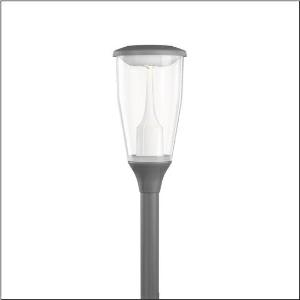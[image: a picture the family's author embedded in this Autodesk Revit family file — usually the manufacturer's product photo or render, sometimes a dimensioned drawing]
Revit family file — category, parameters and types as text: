
# Revit family: dl_11_iq___st1_2a_5xa5565ef14h000022_473d
name_source: partatom
category: Lighting Fixtures
units: mm (PartAtom-declared; Revit-internal decimal feet)

## family parameters
Cut with Voids When Loaded = No
Host = Face
Light Source = No
Part Type = Normal
Room Calculation Point = No
Round Connector Dimension = Use Diameter
Shared = No

## types (1)
- --- (1 x LED, 1560 lm, 10.5 W, 3000K)
    Apparent Load = 11 VA
    CIE Flux Codes = 24 63 94 96 100
    Color Rendering = 70
    Color Temperature = 3000K
    Default Elevation = 1800 mm
    Description = DL 11 iQ, mast luminaire, Module 540 iQ-SR, primary light control with 3 zone facetted reflector, of plastic, silver coated, highly specular, structured, primary optical cover: cover, of PMMA, transparent, light distribution: ST1.2a, light emission: direct distribution, primary light characteristic: asymmetric, installation type: post-top, LED, High Power LED, rated luminous flux: 1.560lm, luminous efficacy: 149lm/W, light colour: 730, colour temperature: 3000K, control: Street-Remote, Auto-Match, Temp-Guard, Lumen-Switch, Night-Set, Smart-Wire, Light-Fading, Desk-Remote (wireless, voltage-free reading and setting of iQ features in the workshop via application-optimized NFC function/RFID function), optimised constant luminous flux control (CLO 2.0), mains connection: 220..240V, AC, 50/60Hz, connection cable pre-assembled, cable length: 5,5m, start of lifetime: 10W, end of service life: 11W, reduction: 5W, luminaire housing, upper part, of diecast aluminium, coated, Siteco® metallic grey (DB 702S), spigot size: 60mm (post-top), post-top mast mounting element, of diecast aluminium, coated, Siteco® metallic grey (DB 702S), Module 540 iQ-SR, traffic white (RAL 9016), equipment: standard, protection rating (complete): IP66, insulation class (complete): insulation class II (safety insulation), certification: CE, ENEC, ENEC+, VDE, packaging unit: 1 piece

Light Distribution: ST1.2a
    Height = 665 mm
    Lamp = 1 x LED
    Lamp Light Flux = 1560 lm
    Lamp Power = 10.5 W
    Lamp count = 1
    Length = 334 mm
    Luminous efficacy = 149 lm/W
    Manufacturer = Siteco
    ModVariant = No
    Model = 5XA5565EF14H000022
    Number of Poles = 1
    OnlyDefault = Yes
    Power Factor = 1
    Product Name = DL 11 iQ | ST1.2a
    Product group = mast luminaire | pylon top
    ProductGroupID = 6100
    Protection Class = Protection class II
    Protection Degree = IP 66
    RLX_Detail_Level = 1
    RLX_Emergency_Light_Flux = 0 lm
    RLX_Emergency_Type = 0
    RLX_Emergency_Type_DB = No
    RlxData = <blob elided: 152157 chars, md5=cda59138>
    Socket = socket
    Standby Power = 0 W
    System Light Flux = 1560 lm
    System Power = 11 W
    Type Comments = factory setting: luminous flux: 100 % | dim-lin: 254 | 419 mA
    Type Image = l_1258354.jpg
    URL = http://relux.com
    VarID = @adj_025903
    Voltage = 0 V
    Weight = 0.00 kg
    Width = 0 mm  [stored 0 ft]

note: [stored X ft] marks values corroborated as IEEE doubles in the binary element streams (Revit-internal decimal feet)

## geometry (parser evidence)
native form markers: Blend x4, Sweep x10
no freeform markers — native parametric forms only
